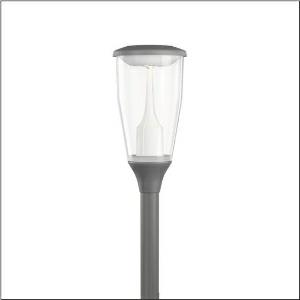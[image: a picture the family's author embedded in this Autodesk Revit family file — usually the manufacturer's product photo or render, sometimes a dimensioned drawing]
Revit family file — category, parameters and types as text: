
# Revit family: dl_11_iq___st1_2a_5xa5565af14h000022_cb01
name_source: partatom
category: Lighting Fixtures
units: mm (PartAtom-declared; Revit-internal decimal feet)

## family parameters
Cut with Voids When Loaded = No
Host = Face
Light Source = No
Part Type = Normal
Room Calculation Point = No
Round Connector Dimension = Use Diameter
Shared = No

## types (1)
- --- (1 x LED, 1560 lm, 12.9 W, 2200K)
    Apparent Load = 13 VA
    CIE Flux Codes = 24 63 94 96 100
    Color Rendering = 70
    Color Temperature = 2200K
    Default Elevation = 1800 mm
    Description = DL 11 iQ, mast luminaire, Module 540 iQ-SR, primary light control with 3 zone facetted reflector, of plastic, silver coated, highly specular, structured, primary optical cover: cover, of PMMA, transparent, light distribution: ST1.2a, light emission: direct distribution, primary light characteristic: asymmetric, installation type: post-top, LED, High Power LED, rated luminous flux: 1.560lm, luminous efficacy: 149lm/W, light colour: 722, colour temperature: 2200K, control gear: iQ Street-Remote, control: Street-Remote, Auto-Match, Temp-Guard, Lumen-Switch, Night-Set, Smart-Wire, Light-Fading, Desk-Remote (wireless, voltage-free reading and setting of iQ features in the workshop via application-optimized NFC function/RFID function), optimised constant luminous flux control (CLO 2.0), mains connection: 220..240V, AC, 50/60Hz, connection cable pre-assembled, cable length: 5,5m, start of lifetime: 13W, end of service life: 13W, reduction: 5W, luminaire housing, upper part, of diecast aluminium, coated, Siteco® metallic grey (DB 702S), spigot size: 60mm (post-top), mounting height: 3..5m, post-top mast mounting element, of diecast aluminium, coated, Siteco® metallic grey (DB 702S), Module 540 iQ-SR, traffic white (RAL 9016), equipment: standard, protection rating (complete): IP66, insulation class (complete): insulation class II (safety insulation), certification: CE, ENEC, ENEC+, VDE, impact resistance: IK07, packaging unit: 1 piece

Light Distribution: ST1.2a
    Height = 665 mm
    Lamp = 1 x LED
    Lamp Light Flux = 1560 lm
    Lamp Power = 12.9 W
    Lamp count = 1
    Length = 334 mm
    Luminous efficacy = 121 lm/W
    Manufacturer = Siteco
    ModVariant = No
    Model = 5XA5565AF14H000022
    Number of Poles = 1
    OnlyDefault = Yes
    Power Factor = 1
    Product Name = DL 11 iQ | ST1.2a
    Product group = mast luminaire | pylon top
    ProductGroupID = 6100
    Protection Class = Protection class II
    Protection Degree = IP 66
    RLX_Detail_Level = 1
    RLX_Emergency_Light_Flux = 0 lm
    RLX_Emergency_Type = 0
    RLX_Emergency_Type_DB = No
    RlxData = <blob elided: 152453 chars, md5=698ec6e1>
    Socket = socket
    Standby Power = 0 W
    System Light Flux = 1560 lm
    System Power = 13 W
    Type Comments = factory setting: luminous flux: 100 % | dim-lin: 254 | 516 mA
    Type Image = l_1258354.jpg
    URL = http://relux.com
    VarID = @adj_095202
    Voltage = 0 V
    Weight = 0.00 kg
    Width = 0 mm  [stored 0 ft]

note: [stored X ft] marks values corroborated as IEEE doubles in the binary element streams (Revit-internal decimal feet)

## geometry (parser evidence)
native form markers: Blend x4, Sweep x12
no freeform markers — native parametric forms only
